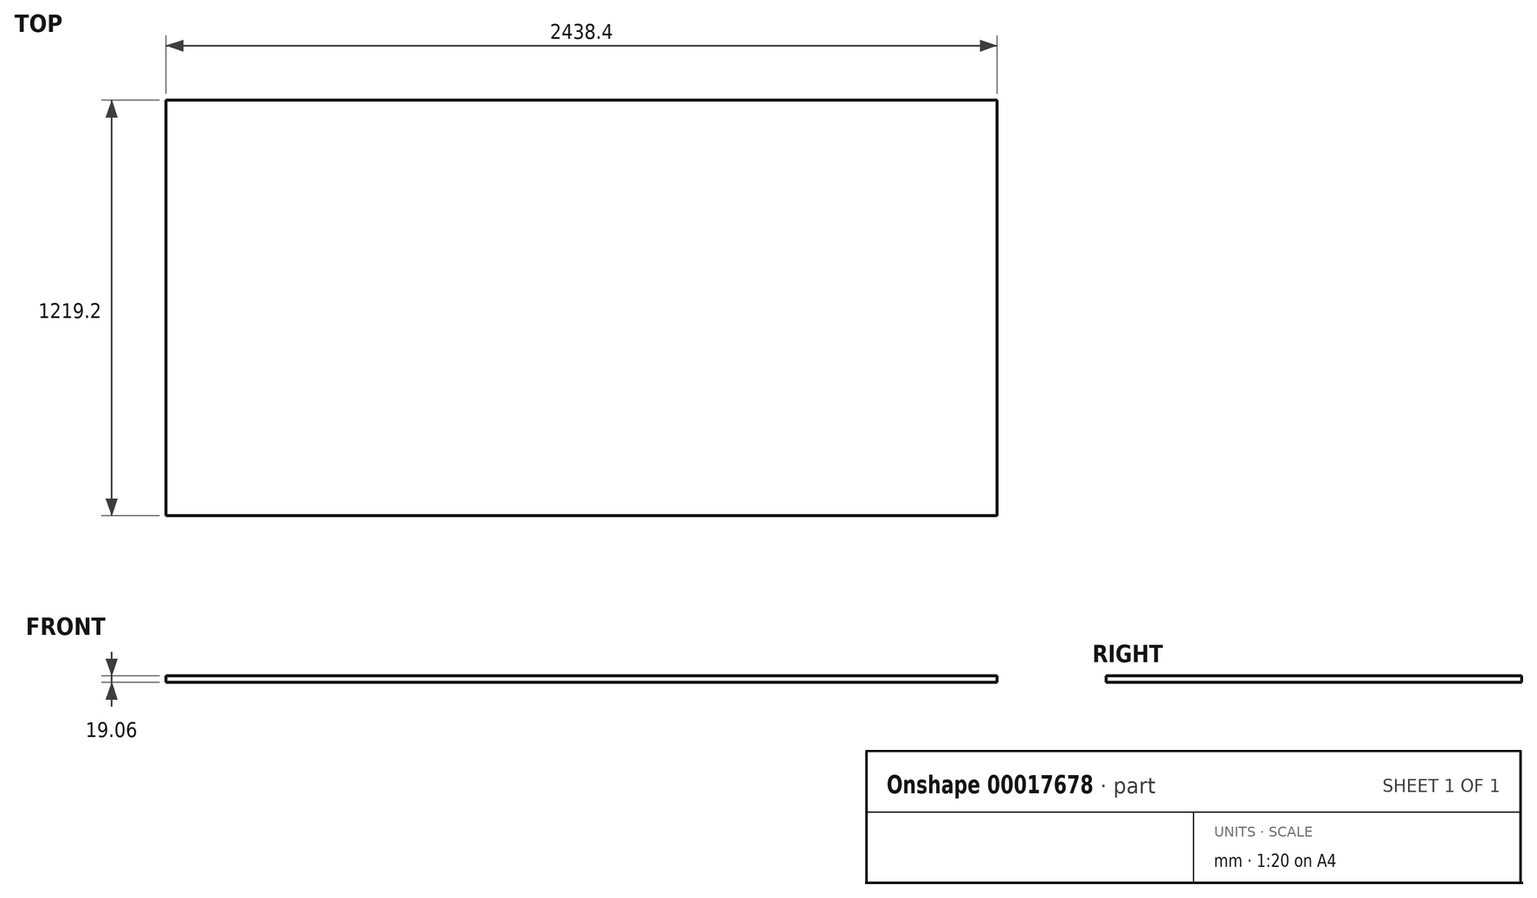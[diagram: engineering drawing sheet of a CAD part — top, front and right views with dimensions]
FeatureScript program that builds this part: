
annotation { "Feature Type Name" : "Feature", "Feature Type Description" : "" }
export const myFeature = defineFeature(function(context is Context, id is Id, definition is map)
    precondition{}
    {
        {
            var Q0;
            Q0=qCreatedBy(makeId("Top.planeOp"),FACE);
            var sketch = newSketch(context, id + "F0", { "sketchPlane" : qUnion([Q0])});
            skLineSegment(sketch, "E0.rect.bottom", {"start": v(1219.2, 609.6) * mm, "end": v(-1219.2, 609.6) * mm});
            skLineSegment(sketch, "E0.rect.top", {"start": v(1219.2, -609.6) * mm, "end": v(-1219.2, -609.6) * mm});
            skLineSegment(sketch, "E0.rect.left", {"start": v(1219.2, 609.6) * mm, "end": v(1219.2, -609.6) * mm});
            skLineSegment(sketch, "E0.rect.right", {"start": v(-1219.2, 609.6) * mm, "end": v(-1219.2, -609.6) * mm});
            skPoint(sketch, "E0.rect.middle", {"position": v(0, 0) * mm});
            skSolve(sketch);
        }
        {
            var Q0;
            Q0 = qSketchRegion(id + "F0", true);
            extrude(context, id + "F1", {"entities" : qUnion([Q0]), "endBound" : BoundingType.SYMMETRIC, "depth" : 19.05 * mm});
        }
    });
